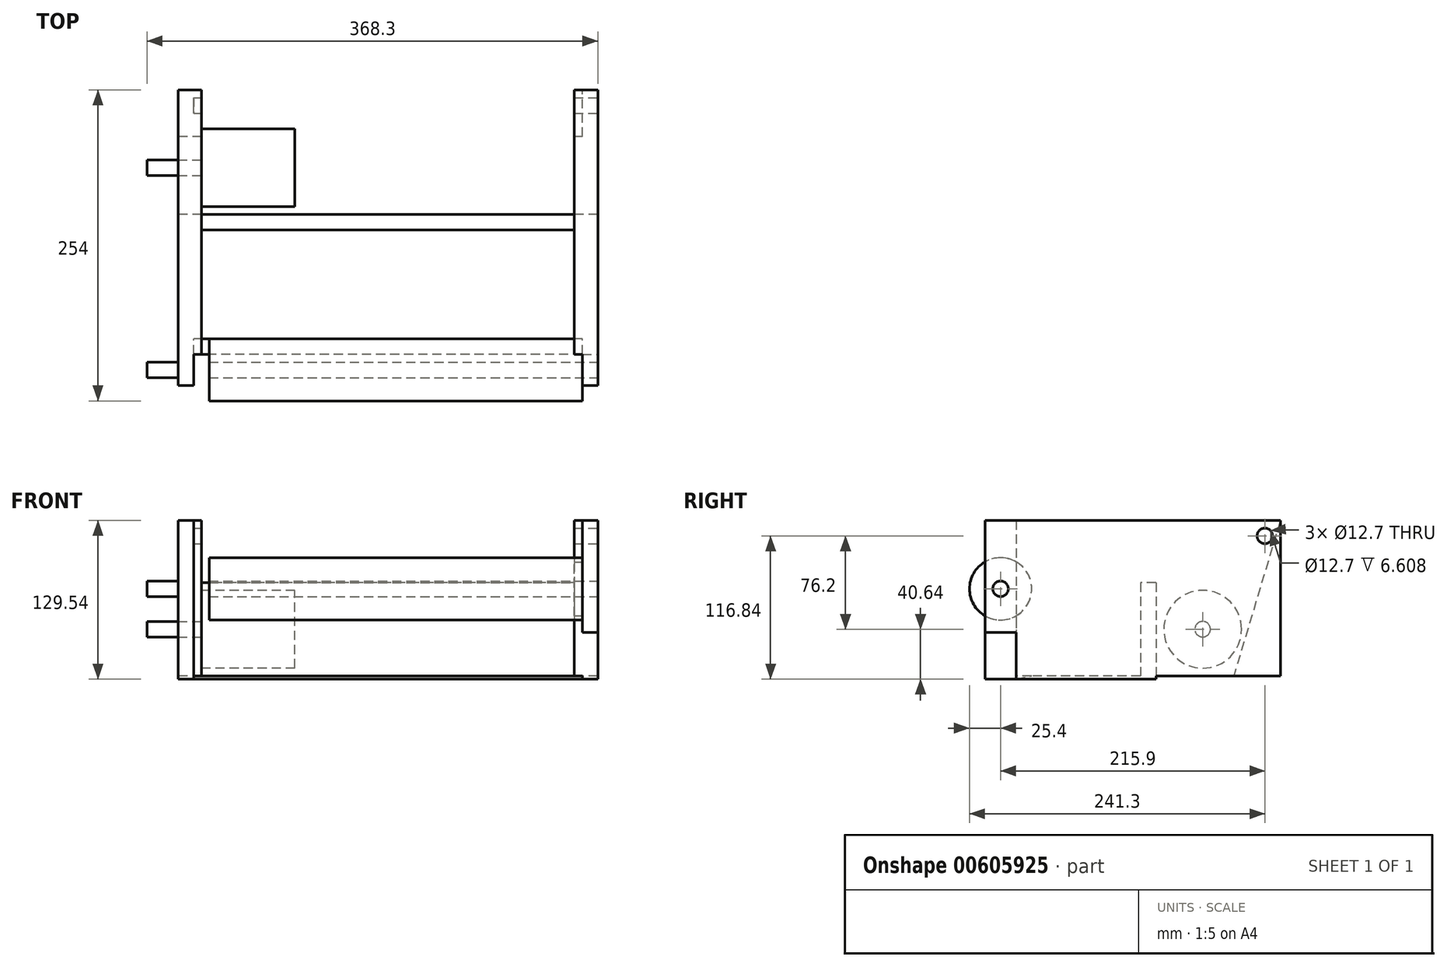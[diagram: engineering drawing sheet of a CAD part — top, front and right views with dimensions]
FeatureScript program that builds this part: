
annotation { "Feature Type Name" : "Feature", "Feature Type Description" : "" }
export const myFeature = defineFeature(function(context is Context, id is Id, definition is map)
    precondition{}
    {
        {
            var Q0;
            Q0=qCreatedBy(makeId("Right.planeOp"),FACE);
            var sketch = newSketch(context, id + "F0", { "sketchPlane" : qUnion([Q0])});
            skLineSegment(sketch, "E0.bottom", {"start": v(57.15, 1.27) * mm, "end": v(-44.45, 1.27) * mm});
            skLineSegment(sketch, "E0.top", {"start": v(57.15, -1.27) * mm, "end": v(-57.15, -1.27) * mm});
            skLineSegment(sketch, "E0.left", {"start": v(57.15, 1.27) * mm, "end": v(57.15, -1.27) * mm});
            skPoint(sketch, "E0.middle", {"position": v(0, 0) * mm});
            skLineSegment(sketch, "E1", {"start": v(-57.15, -1.27) * mm, "end": v(-44.45, 1.27) * mm});
            skSolve(sketch);
        }
        {
            var Q0;
            Q0=makeQuery(id+"F0.imprint","IMPRINT",FACE,{"disambiguationData":[TD([[makeQuery(id+"F0.imprint","IMPRINT",EDGE,{"derivedFrom":sQuery(id+"F0.wireOp",EDGE,"E0.bottom")}),1.0]])]});
            extrude(context, id + "F1", {"entities" : qUnion([Q0]), "endBound" : BoundingType.SYMMETRIC, "depth" : 317.5 * mm, "offsetDistance" : 25.4 * mm});
        }
        {
            var Q0;
            Q0=makeQuery(id+"F1.opExtrude","CAP_FACE",FACE,{"disambiguationData":[OSD([sQuery(id+"F0.wireOp",EDGE,"E0.bottom"),sQuery(id+"F0.wireOp",EDGE,"E0.top"),sQuery(id+"F0.wireOp",EDGE,"E0.left"),sQuery(id+"F0.wireOp",EDGE,"E1")])],"isStart":false});
            var sketch = newSketch(context, id + "F2", { "sketchPlane" : qUnion([Q0])});
            skLineSegment(sketch, "E2.bottom", {"start": v(-57.15, 1.27) * mm, "end": v(57.15, 1.27) * mm});
            skLineSegment(sketch, "E2.top", {"start": v(-57.15, -1.27) * mm, "end": v(57.15, -1.27) * mm});
            skLineSegment(sketch, "E2.left", {"start": v(-57.15, 1.27) * mm, "end": v(-57.15, -1.27) * mm});
            skLineSegment(sketch, "E2.right", {"start": v(57.15, 1.27) * mm, "end": v(57.15, -1.27) * mm});
            skSolve(sketch);
        }
        {
            var Q0;
            Q0 = qSketchRegion(id + "F2", true);
            extrude(context, id + "F3", {"entities" : qUnion([Q0]), "operationType" : NewBodyOperationType.ADD, "depth" : 12.7 * mm, "offsetDistance" : 25.4 * mm});
        }
        {
            var Q0;
            Q0=makeQuery(id+"F1.opExtrude","SWEPT_BODY",BODY,{"disambiguationData":[OSD([sQuery(id+"F0.wireOp",EDGE,"E0.bottom"),sQuery(id+"F0.wireOp",EDGE,"E0.top"),sQuery(id+"F0.wireOp",EDGE,"E0.left"),sQuery(id+"F0.wireOp",EDGE,"E1")])]});
            var Q1;
            Q1=qCreatedBy(makeId("Right.planeOp"),FACE);
            mirror(context, id + "F4", {"operationType" : NewBodyOperationType.ADD, "entities" : qUnion([Q0]), "mirrorPlane" : qUnion([Q1])});
        }
        {
            var Q0;
            {var subQ0=makeQuery(id+"F3.boolean.opBoolean","MERGE",FACE,{"derivedFrom":[makeQuery(id+"F1.opExtrude","SWEPT_FACE",FACE,{"disambiguationData":[OSD([sQuery(id+"F0.wireOp",EDGE,"E0.bottom")])]}),makeQuery(id+"F3.opExtrude","SWEPT_FACE",FACE,{"disambiguationData":[OSD([sQuery(id+"F2.wireOp",EDGE,"E2.bottom")])]})]});Q0=makeQuery(id+"F4.boolean.opBoolean","MERGE",FACE,{"derivedFrom":[subQ0,makeQuery(id+"F4.opPattern","COPY",FACE,{"derivedFrom":subQ0,"instanceName":"1"})]});}
            var sketch = newSketch(context, id + "F5", { "sketchPlane" : qUnion([Q0])});
            skLineSegment(sketch, "E3.top", {"start": v(-171.45, -57.15) * mm, "end": v(-152.14, -57.15) * mm});
            skLineSegment(sketch, "E3.left", {"start": v(-171.45, 57.15) * mm, "end": v(-171.45, -57.15) * mm});
            skLineSegment(sketch, "E3.right", {"start": v(-152.14, 158.75) * mm, "end": v(-152.14, -57.15) * mm});
            skLineSegment(sketch, "E4.MirrorCS", {"start": v(152.14, 158.75) * mm, "end": v(152.14, -57.15) * mm});
            skLineSegment(sketch, "E5.MirrorCS", {"start": v(171.45, 57.15) * mm, "end": v(171.45, -57.15) * mm});
            skLineSegment(sketch, "E6.MirrorCS", {"start": v(171.45, -57.15) * mm, "end": v(152.14, -57.15) * mm});
            skLineSegment(sketch, "E7", {"start": v(-171.45, 57.15) * mm, "end": v(-171.45, 158.75) * mm});
            skLineSegment(sketch, "E8", {"start": v(-171.45, 158.75) * mm, "end": v(-158.75, 158.75) * mm});
            skLineSegment(sketch, "E9", {"start": v(-158.75, 158.75) * mm, "end": v(-152.14, 158.75) * mm});
            skPoint(sketch, "E10.MirrorCS.end.orphan", {"position": v(152.14, 158.75) * mm});
            skPoint(sketch, "E10.MirrorCS.start.orphan", {"position": v(171.45, 57.15) * mm});
            skLineSegment(sketch, "E11", {"start": v(171.45, 57.15) * mm, "end": v(171.45, 158.75) * mm});
            skLineSegment(sketch, "E12", {"start": v(171.45, 158.75) * mm, "end": v(152.14, 158.75) * mm});
            skSolve(sketch);
        }
        {
            var Q0;
            Q0 = qSketchRegion(id + "F5", true);
            extrude(context, id + "F6", {"entities" : qUnion([Q0]), "operationType" : NewBodyOperationType.ADD, "depth" : 127 * mm, "offsetDistance" : 25.4 * mm});
        }
        {
            var Q0;
            Q0=makeQuery(id+"F6.boolean.opBoolean","MERGE",FACE,{"derivedFrom":[makeQuery(id+"F4.opPattern","COPY",FACE,{"derivedFrom":makeQuery(id+"F3.opExtrude","SWEPT_FACE",FACE,{"disambiguationData":[OSD([sQuery(id+"F2.wireOp",EDGE,"E2.left")])]}),"instanceName":"1"}),makeQuery(id+"F6.opExtrude","SWEPT_FACE",FACE,{"disambiguationData":[OSD([sQuery(id+"F5.wireOp",EDGE,"E3.top")])]})]});
            var sketch = newSketch(context, id + "F7", { "sketchPlane" : qUnion([Q0])});
            skLineSegment(sketch, "E13.bottom", {"start": v(-171.45, 128.27) * mm, "end": v(-158.75, 128.27) * mm});
            skLineSegment(sketch, "E13.top", {"start": v(-171.45, -1.27) * mm, "end": v(-158.75, -1.27) * mm});
            skLineSegment(sketch, "E13.left", {"start": v(-171.45, 128.27) * mm, "end": v(-171.45, -1.27) * mm});
            skLineSegment(sketch, "E13.right", {"start": v(-158.75, 128.27) * mm, "end": v(-158.75, -1.27) * mm});
            skLineSegment(sketch, "E14.MirrorCS", {"start": v(171.45, 128.27) * mm, "end": v(158.75, 128.27) * mm});
            skLineSegment(sketch, "E15.MirrorCS", {"start": v(158.75, 128.27) * mm, "end": v(158.75, -1.27) * mm});
            skLineSegment(sketch, "E16.MirrorCS", {"start": v(171.45, 128.27) * mm, "end": v(171.45, -1.27) * mm});
            skLineSegment(sketch, "E17.MirrorCS", {"start": v(171.45, -1.27) * mm, "end": v(158.75, -1.27) * mm});
            skSolve(sketch);
        }
        {
            var Q0;
            Q0 = qSketchRegion(id + "F7", true);
            extrude(context, id + "F8", {"entities" : qUnion([Q0]), "operationType" : NewBodyOperationType.ADD, "depth" : 25.4 * mm, "offsetDistance" : 25.4 * mm});
        }
        {
            var Q0;
            Q0=makeQuery(id+"F8.boolean.opBoolean","MERGE",FACE,{"derivedFrom":[makeQuery(id+"F6.boolean.opBoolean","MERGE",FACE,{"derivedFrom":[makeQuery(id+"F3.opExtrude","CAP_FACE",FACE,{"disambiguationData":[OSD([sQuery(id+"F2.wireOp",EDGE,"E2.bottom"),sQuery(id+"F2.wireOp",EDGE,"E2.top"),sQuery(id+"F2.wireOp",EDGE,"E2.left"),sQuery(id+"F2.wireOp",EDGE,"E2.right")])],"isStart":true}),makeQuery(id+"F6.opExtrude","SWEPT_FACE",FACE,{"disambiguationData":[OSD([sQuery(id+"F5.wireOp",EDGE,"E4.MirrorCS")])]})]}),makeQuery(id+"F8.opExtrude","SWEPT_FACE",FACE,{"disambiguationData":[OSD([sQuery(id+"F7.wireOp",EDGE,"E15.MirrorCS")])]})]});
            var sketch = newSketch(context, id + "F9", { "sketchPlane" : qUnion([Q0])});
            skCircle(sketch, "E18", {"center": v(69.85, 72.39) * mm, "radius": 25.4 * mm});
            skCircle(sketch, "E19", {"center": v(69.85, 72.39) * mm, "radius": 6.35 * mm});
            skSolve(sketch);
        }
        {
            var Q0;
            Q0 = qSketchRegion(id + "F9", true);
            extrude(context, id + "F10", {"entities" : qUnion([Q0]), "operationType" : NewBodyOperationType.ADD, "depth" : 304.8 * mm, "offsetDistance" : 25.4 * mm});
        }
        {
            var Q0;
            Q0=makeQuery(id+"F8.boolean.opBoolean","MERGE",FACE,{"derivedFrom":[makeQuery(id+"F6.boolean.opBoolean","MERGE",FACE,{"derivedFrom":[makeQuery(id+"F3.opExtrude","CAP_FACE",FACE,{"disambiguationData":[OSD([sQuery(id+"F2.wireOp",EDGE,"E2.bottom"),sQuery(id+"F2.wireOp",EDGE,"E2.top"),sQuery(id+"F2.wireOp",EDGE,"E2.left"),sQuery(id+"F2.wireOp",EDGE,"E2.right")])],"isStart":false}),makeQuery(id+"F6.opExtrude","SWEPT_FACE",FACE,{"disambiguationData":[OSD([sQuery(id+"F5.wireOp",EDGE,"E5.MirrorCS")])]})]}),makeQuery(id+"F8.opExtrude","SWEPT_FACE",FACE,{"disambiguationData":[OSD([sQuery(id+"F7.wireOp",EDGE,"E16.MirrorCS")])]})]});
            var sketch = newSketch(context, id + "F11", { "sketchPlane" : qUnion([Q0])});
            skCircle(sketch, "E20", {"center": v(-69.85, 72.39) * mm, "radius": 6.35 * mm});
            skSolve(sketch);
        }
        {
            var Q0;
            Q0 = qSketchRegion(id + "F11", true);
            extrude(context, id + "F12", {"entities" : qUnion([Q0]), "operationType" : NewBodyOperationType.REMOVE, "oppositeDirection" : true, "depth" : 330.2 * mm, "offsetDistance" : 25.4 * mm});
        }
        {
            var Q0;
            {var subQ0=makeQuery(id+"F3.boolean.opBoolean","MERGE",FACE,{"derivedFrom":[makeQuery(id+"F1.opExtrude","SWEPT_FACE",FACE,{"disambiguationData":[OSD([sQuery(id+"F0.wireOp",EDGE,"E0.bottom")])]}),makeQuery(id+"F3.opExtrude","SWEPT_FACE",FACE,{"disambiguationData":[OSD([sQuery(id+"F2.wireOp",EDGE,"E2.bottom")])]})]});Q0=makeQuery(id+"F4.boolean.opBoolean","MERGE",FACE,{"derivedFrom":[subQ0,makeQuery(id+"F4.opPattern","COPY",FACE,{"derivedFrom":subQ0,"instanceName":"1"})]});}
            var sketch = newSketch(context, id + "F13", { "sketchPlane" : qUnion([Q0])});
            skLineSegment(sketch, "E21.bottom", {"start": v(-152.14, 57.15) * mm, "end": v(152.14, 57.15) * mm});
            skLineSegment(sketch, "E21.top", {"start": v(-152.14, 44.45) * mm, "end": v(152.14, 44.45) * mm});
            skLineSegment(sketch, "E21.left", {"start": v(-152.14, 57.15) * mm, "end": v(-152.14, 44.45) * mm});
            skLineSegment(sketch, "E21.right", {"start": v(152.14, 57.15) * mm, "end": v(152.14, 44.45) * mm});
            skSolve(sketch);
        }
        {
            var Q0;
            Q0 = qSketchRegion(id + "F13", true);
            extrude(context, id + "F14", {"entities" : qUnion([Q0]), "operationType" : NewBodyOperationType.ADD, "depth" : 76.2 * mm, "offsetDistance" : 25.4 * mm});
        }
        {
            var Q0;
            Q0=makeQuery(id+"F8.boolean.opBoolean","MERGE",FACE,{"derivedFrom":[makeQuery(id+"F6.boolean.opBoolean","MERGE",FACE,{"derivedFrom":[makeQuery(id+"F3.opExtrude","CAP_FACE",FACE,{"disambiguationData":[OSD([sQuery(id+"F2.wireOp",EDGE,"E2.bottom"),sQuery(id+"F2.wireOp",EDGE,"E2.top"),sQuery(id+"F2.wireOp",EDGE,"E2.left"),sQuery(id+"F2.wireOp",EDGE,"E2.right")])],"isStart":false}),makeQuery(id+"F6.opExtrude","SWEPT_FACE",FACE,{"disambiguationData":[OSD([sQuery(id+"F5.wireOp",EDGE,"E5.MirrorCS"),sQuery(id+"F5.wireOp",EDGE,"E11")])]})]}),makeQuery(id+"F8.opExtrude","SWEPT_FACE",FACE,{"disambiguationData":[OSD([sQuery(id+"F7.wireOp",EDGE,"E16.MirrorCS")])]})]});
            var sketch = newSketch(context, id + "F15", { "sketchPlane" : qUnion([Q0])});
            skLineSegment(sketch, "E22.bottom", {"start": v(-82.55, -1.27) * mm, "end": v(-57.15, -1.27) * mm});
            skLineSegment(sketch, "E22.top", {"start": v(-82.55, 36.83) * mm, "end": v(-57.15, 36.83) * mm});
            skLineSegment(sketch, "E22.left", {"start": v(-82.55, -1.27) * mm, "end": v(-82.55, 36.83) * mm});
            skLineSegment(sketch, "E22.right", {"start": v(-57.15, -1.27) * mm, "end": v(-57.15, 36.83) * mm});
            skSolve(sketch);
        }
        {
            var Q0;
            Q0 = qSketchRegion(id + "F15", true);
            extrude(context, id + "F16", {"entities" : qUnion([Q0]), "operationType" : NewBodyOperationType.REMOVE, "oppositeDirection" : true, "depth" : 330.2 * mm, "offsetDistance" : 25.4 * mm});
        }
        {
            var Q0;
            Q0=makeQuery(id+"F6.opExtrude","SWEPT_FACE",FACE,{"disambiguationData":[OSD([sQuery(id+"F5.wireOp",EDGE,"E3.right")])]});
            var sketch = newSketch(context, id + "F17", { "sketchPlane" : qUnion([Q0])});
            skCircle(sketch, "E23", {"center": v(95.25, 39.37) * mm, "radius": 6.35 * mm});
            skSolve(sketch);
        }
        {
            var Q0;
            Q0 = qSketchRegion(id + "F17", true);
            extrude(context, id + "F18", {"entities" : qUnion([Q0]), "operationType" : NewBodyOperationType.REMOVE, "oppositeDirection" : true, "depth" : 25.4 * mm, "offsetDistance" : 25.4 * mm});
        }
        {
            var Q0;
            Q0=makeQuery(id+"F8.boolean.opBoolean","MERGE",FACE,{"derivedFrom":[makeQuery(id+"F6.boolean.opBoolean","MERGE",FACE,{"derivedFrom":[makeQuery(id+"F4.opPattern","COPY",FACE,{"derivedFrom":makeQuery(id+"F3.opExtrude","CAP_FACE",FACE,{"disambiguationData":[OSD([sQuery(id+"F2.wireOp",EDGE,"E2.bottom"),sQuery(id+"F2.wireOp",EDGE,"E2.top"),sQuery(id+"F2.wireOp",EDGE,"E2.left"),sQuery(id+"F2.wireOp",EDGE,"E2.right")])],"isStart":false}),"instanceName":"1"}),makeQuery(id+"F6.opExtrude","SWEPT_FACE",FACE,{"disambiguationData":[OSD([sQuery(id+"F5.wireOp",EDGE,"E3.left"),sQuery(id+"F5.wireOp",EDGE,"E7")])]})]}),makeQuery(id+"F8.opExtrude","SWEPT_FACE",FACE,{"disambiguationData":[OSD([sQuery(id+"F7.wireOp",EDGE,"E13.left")])]})]});
            var sketch = newSketch(context, id + "F19", { "sketchPlane" : qUnion([Q0])});
            skCircle(sketch, "E24", {"center": v(-95.25, 39.37) * mm, "radius": 6.35 * mm});
            skCircle(sketch, "E25", {"center": v(69.85, 72.39) * mm, "radius": 6.35 * mm});
            skSolve(sketch);
        }
        {
            var Q0;
            Q0 = qSketchRegion(id + "F19", true);
            extrude(context, id + "F20", {"entities" : qUnion([Q0]), "depth" : 25.4 * mm, "offsetDistance" : 25.4 * mm});
        }
        {
            var Q0;
            Q0=makeQuery(id+"F6.opExtrude","SWEPT_FACE",FACE,{"disambiguationData":[OSD([sQuery(id+"F5.wireOp",EDGE,"E3.right")])]});
            var sketch = newSketch(context, id + "F21", { "sketchPlane" : qUnion([Q0])});
            skCircle(sketch, "E26", {"center": v(95.25, 39.37) * mm, "radius": 31.75 * mm});
            skSolve(sketch);
        }
        {
            var Q0;
            Q0 = qSketchRegion(id + "F21", true);
            extrude(context, id + "F22", {"entities" : qUnion([Q0]), "depth" : 76.2 * mm, "offsetDistance" : 25.4 * mm});
        }
        {
            var Q0;
            Q0=makeQuery(id+"F8.boolean.opBoolean","MERGE",FACE,{"derivedFrom":[makeQuery(id+"F6.boolean.opBoolean","MERGE",FACE,{"derivedFrom":[makeQuery(id+"F3.opExtrude","CAP_FACE",FACE,{"disambiguationData":[OSD([sQuery(id+"F2.wireOp",EDGE,"E2.bottom"),sQuery(id+"F2.wireOp",EDGE,"E2.top"),sQuery(id+"F2.wireOp",EDGE,"E2.left"),sQuery(id+"F2.wireOp",EDGE,"E2.right")])],"isStart":false}),makeQuery(id+"F6.opExtrude","SWEPT_FACE",FACE,{"disambiguationData":[OSD([sQuery(id+"F5.wireOp",EDGE,"E5.MirrorCS"),sQuery(id+"F5.wireOp",EDGE,"E11")])]})]}),makeQuery(id+"F8.opExtrude","SWEPT_FACE",FACE,{"disambiguationData":[OSD([sQuery(id+"F7.wireOp",EDGE,"E16.MirrorCS")])]})]});
            var sketch = newSketch(context, id + "F23", { "sketchPlane" : qUnion([Q0])});
            skCircle(sketch, "E27", {"center": v(146.05, 115.57) * mm, "radius": 6.35 * mm});
            skSolve(sketch);
        }
        {
            var Q0;
            Q0 = qSketchRegion(id + "F23", true);
            extrude(context, id + "F24", {"entities" : qUnion([Q0]), "operationType" : NewBodyOperationType.REMOVE, "oppositeDirection" : true, "depth" : 330.2 * mm, "offsetDistance" : 25.4 * mm});
        }
        {
            var Q0;
            Q0=makeQuery(id+"F8.boolean.opBoolean","MERGE",FACE,{"derivedFrom":[makeQuery(id+"F6.boolean.opBoolean","MERGE",FACE,{"derivedFrom":[makeQuery(id+"F4.opPattern","COPY",FACE,{"derivedFrom":makeQuery(id+"F3.opExtrude","CAP_FACE",FACE,{"disambiguationData":[OSD([sQuery(id+"F2.wireOp",EDGE,"E2.bottom"),sQuery(id+"F2.wireOp",EDGE,"E2.top"),sQuery(id+"F2.wireOp",EDGE,"E2.left"),sQuery(id+"F2.wireOp",EDGE,"E2.right")])],"isStart":false}),"instanceName":"1"}),makeQuery(id+"F6.opExtrude","SWEPT_FACE",FACE,{"disambiguationData":[OSD([sQuery(id+"F5.wireOp",EDGE,"E3.left"),sQuery(id+"F5.wireOp",EDGE,"E7")])]})]}),makeQuery(id+"F8.opExtrude","SWEPT_FACE",FACE,{"disambiguationData":[OSD([sQuery(id+"F7.wireOp",EDGE,"E13.left")])]})]});
            var sketch = newSketch(context, id + "F25", { "sketchPlane" : qUnion([Q0])});
            skLineSegment(sketch, "E28", {"start": v(-120.65, 1.27) * mm, "end": v(-158.75, 128.27) * mm});
            skLineSegment(sketch, "E29", {"start": v(-158.75, 1.27) * mm, "end": v(-158.75, 128.27) * mm});
            skLineSegment(sketch, "E30", {"start": v(-158.75, 1.27) * mm, "end": v(-120.65, 1.27) * mm});
            skSolve(sketch);
        }
        {
            var Q0;
            Q0 = qSketchRegion(id + "F25", true);
            extrude(context, id + "F26", {"entities" : qUnion([Q0]), "operationType" : NewBodyOperationType.REMOVE, "oppositeDirection" : true, "depth" : 330.2 * mm, "offsetDistance" : 25.4 * mm});
        }
    });
